# Revit family: STS_10427_RV17_LOD400
name_source: partatom
category: Электрооборудование
revit_build: Autodesk Revit 2017 (Build: 20170118_1100(x64)
units: mm (PartAtom-declared; Revit-internal decimal feet)

## family parameters
Всегда вертикально = Да
Конфигурация панели = Два столбца, слева направо
На основе рабочей плоскости = Нет
Общий = Нет
При загрузке вырезать с полостями = Нет
Размер круглого соединителя = Использовать диаметр
Тип детали = Щит
Точка расчета площади = Нет

## types (2) — shared parameters
ADSK_URL страницы изделия = https://stilsoft.ru
ADSK_Единица измерения = шт.
ADSK_Завод-изготовитель = ООО «Основа Безопасности»
ADSK_Количество = 1
ADSK_Масса = 102
ADSK_Размер_Высота = 1433 мм
ADSK_Размер_Глубина = 800 мм
ADSK_Размер_Ширина = 600 мм
Диапазон рабочих температур, <unrecoverable-encoding: 5 bytes ef82b0d0a1> = от +5 до +50

## per-type parameters (varying)
| type | ADSK_Марка | ADSK_Наименование | высота, U |
| STS-10412 | СТВФ.426479.065 | Шкаф серверный защищенный STS-10412 | 12 |
| STS-10427 | СТВФ.426479.069 | Шкаф серверный защищенный STS-10427 | 27 |
